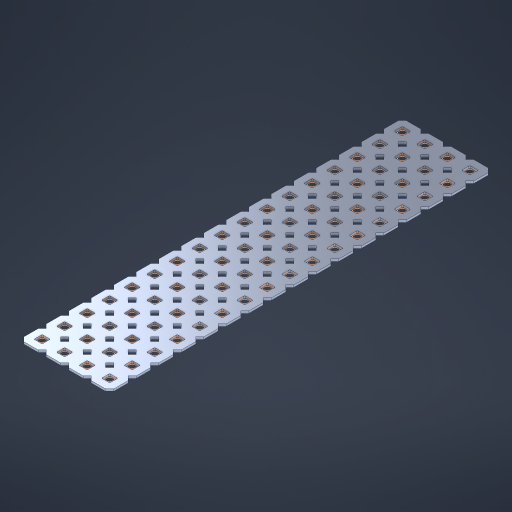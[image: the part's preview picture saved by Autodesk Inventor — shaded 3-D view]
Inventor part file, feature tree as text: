
AUTODESK INVENTOR PART (.ipt)
format: ipt  version: 2023 (Build 270158000, 158)  size: 1,048,064 bytes
history: native  units: in
note: dims shown in document units (in); Inventor stores cm internally (conversion verified against a paired STEP export)
features: other x69, extrude x67, sketch x2, pattern_linear x1
ambient origin geometry x8: Origin, YZ Plane, XZ Plane, XY Plane, X Axis, Y Axis, Z Axis, Center Point
bodies: Solid1 (feature_tree), Body (feature_tree)
feature tree (139):
  pattern_linear  "Rectangular Pattern1"  Spacing1=0.09in  [1 undecoded]
  sketch  "Sketch1"  dims[d1=0.5in]
  sketch  "Sketch2"  dims[d2=0.182in d3=0.09in d4=0.09in d5=0.09in d6=0.09in d7=0.09in d8=0.09in d9=0.09in d10=0.09in d11=0.02in d13=0.0in d14=0.172in d15=0.0625in d16=0.0in d19=0.5in d22=0.5in]
  other  "Srf1"
  other  "Srf126"
  other  "Srf127"
  other  "Srf128"
  other  "Srf129"
  other  "Srf130"
  other  "Srf131"
  other  "Srf250"
  other  "Srf251"
  other  "Srf252"
  other  "Srf253"
  other  "Srf254"
  other  "Srf255"
  other  "Srf256"
  other  "Srf257"
  other  "Srf258"
  other  "Srf259"
  other  "Srf268"
  other  "Srf269"
  other  "Srf270"
  other  "Srf271"
  other  "Srf272"
  other  "Srf273"
  other  "Srf274"
  other  "Srf275"
  other  "Srf276"
  other  "Srf277"
  other  "Srf278"
  other  "Srf279"
  other  "Srf280"
  other  "Srf281"
  other  "Srf282"
  other  "Srf283"
  other  "Srf284"
  other  "Srf293"
  other  "Srf294"
  other  "Srf295"
  other  "Srf296"
  other  "Srf297"
  other  "Srf298"
  other  "Srf299"
  other  "Srf300"
  other  "Srf301"
  other  "Srf302"
  other  "Srf303"
  other  "Srf304"
  other  "Srf305"
  other  "Srf306"
  other  "Srf307"
  other  "Srf308"
  other  "Srf309"
  other  "Srf318"
  other  "Srf319"
  other  "Srf320"
  other  "Srf321"
  other  "Srf322"
  other  "Srf323"
  other  "Srf324"
  other  "Srf325"
  other  "Srf326"
  other  "Srf327"
  other  "Srf328"
  other  "Srf329"
  other  "Srf330"
  other  "Srf331"
  other  "Srf332"
  other  "Srf333"
  other  "Srf334"
  other  "Circle"
  extrude  "ExtrusionSrf126"  Depth=0.09in
  extrude  "ExtrusionSrf127"  Depth=0.09in
  extrude  "ExtrusionSrf128"  Depth=0.09in
  extrude  "ExtrusionSrf129"  Depth=0.09in
  extrude  "ExtrusionSrf130"  Depth=0.09in
  extrude  "ExtrusionSrf131"  Depth=0.09in
  extrude  "ExtrusionSrf250"  Depth=0.09in
  extrude  "ExtrusionSrf251"  Depth=0.02in
  extrude  "ExtrusionSrf252"  TaperAngle=0.0deg  [1 undecoded]
  extrude  "ExtrusionSrf253"  Depth=0.5in
  extrude  "ExtrusionSrf254"  Depth=0.5in TaperAngle=0.0deg
  extrude  "ExtrusionSrf255"  Depth=0.5in
  extrude  "ExtrusionSrf256"  Depth=0.5in
  extrude  "ExtrusionSrf257"  [1 undecoded]
  extrude  "ExtrusionSrf258"  [1 undecoded]
  extrude  "ExtrusionSrf259"  [1 undecoded]
  extrude  "ExtrusionSrf268"  [1 undecoded]
  extrude  "ExtrusionSrf269"  [1 undecoded]
  extrude  "ExtrusionSrf270"  [1 undecoded]
  extrude  "ExtrusionSrf271"  [1 undecoded]
  extrude  "ExtrusionSrf272"  [1 undecoded]
  extrude  "ExtrusionSrf273"  [1 undecoded]
  extrude  "ExtrusionSrf274"  [1 undecoded]
  extrude  "ExtrusionSrf275"  [1 undecoded]
  extrude  "ExtrusionSrf276"  [1 undecoded]
  extrude  "ExtrusionSrf277"  [1 undecoded]
  extrude  "ExtrusionSrf278"  [1 undecoded]
  extrude  "ExtrusionSrf279"  [1 undecoded]
  extrude  "ExtrusionSrf280"  [1 undecoded]
  extrude  "ExtrusionSrf281"  [1 undecoded]
  extrude  "ExtrusionSrf282"  [1 undecoded]
  extrude  "ExtrusionSrf283"  [1 undecoded]
  extrude  "ExtrusionSrf284"  [1 undecoded]
  extrude  "ExtrusionSrf293"  [1 undecoded]
  extrude  "ExtrusionSrf294"  [1 undecoded]
  extrude  "ExtrusionSrf295"  [1 undecoded]
  extrude  "ExtrusionSrf296"  [1 undecoded]
  extrude  "ExtrusionSrf297"  [1 undecoded]
  extrude  "ExtrusionSrf298"  [1 undecoded]
  extrude  "ExtrusionSrf299"  [1 undecoded]
  extrude  "ExtrusionSrf300"  [1 undecoded]
  extrude  "ExtrusionSrf301"  [1 undecoded]
  extrude  "ExtrusionSrf302"  [1 undecoded]
  extrude  "ExtrusionSrf303"  [1 undecoded]
  extrude  "ExtrusionSrf304"  [1 undecoded]
  extrude  "ExtrusionSrf305"  [1 undecoded]
  extrude  "ExtrusionSrf306"  [1 undecoded]
  extrude  "ExtrusionSrf307"  [1 undecoded]
  extrude  "ExtrusionSrf308"  [1 undecoded]
  extrude  "ExtrusionSrf309"  [1 undecoded]
  extrude  "ExtrusionSrf318"  [1 undecoded]
  extrude  "ExtrusionSrf319"  [1 undecoded]
  extrude  "ExtrusionSrf320"  [1 undecoded]
  extrude  "ExtrusionSrf321"  [1 undecoded]
  extrude  "ExtrusionSrf322"  [1 undecoded]
  extrude  "ExtrusionSrf323"  [1 undecoded]
  extrude  "ExtrusionSrf324"  [1 undecoded]
  extrude  "ExtrusionSrf325"  [1 undecoded]
  extrude  "ExtrusionSrf326"  [1 undecoded]
  extrude  "ExtrusionSrf327"  [1 undecoded]
  extrude  "ExtrusionSrf328"  [1 undecoded]
  extrude  "ExtrusionSrf329"  [1 undecoded]
  extrude  "ExtrusionSrf330"  [1 undecoded]
  extrude  "ExtrusionSrf331"  [1 undecoded]
  extrude  "ExtrusionSrf332"  [1 undecoded]
  extrude  "ExtrusionSrf333"  [1 undecoded]
  extrude  "ExtrusionSrf334"  [1 undecoded]
note: 56 required parameter values undecoded (feature->parameter linkage not recoverable at this tier; creation-order binding heuristic only, values carry confidence <= 0.55)
